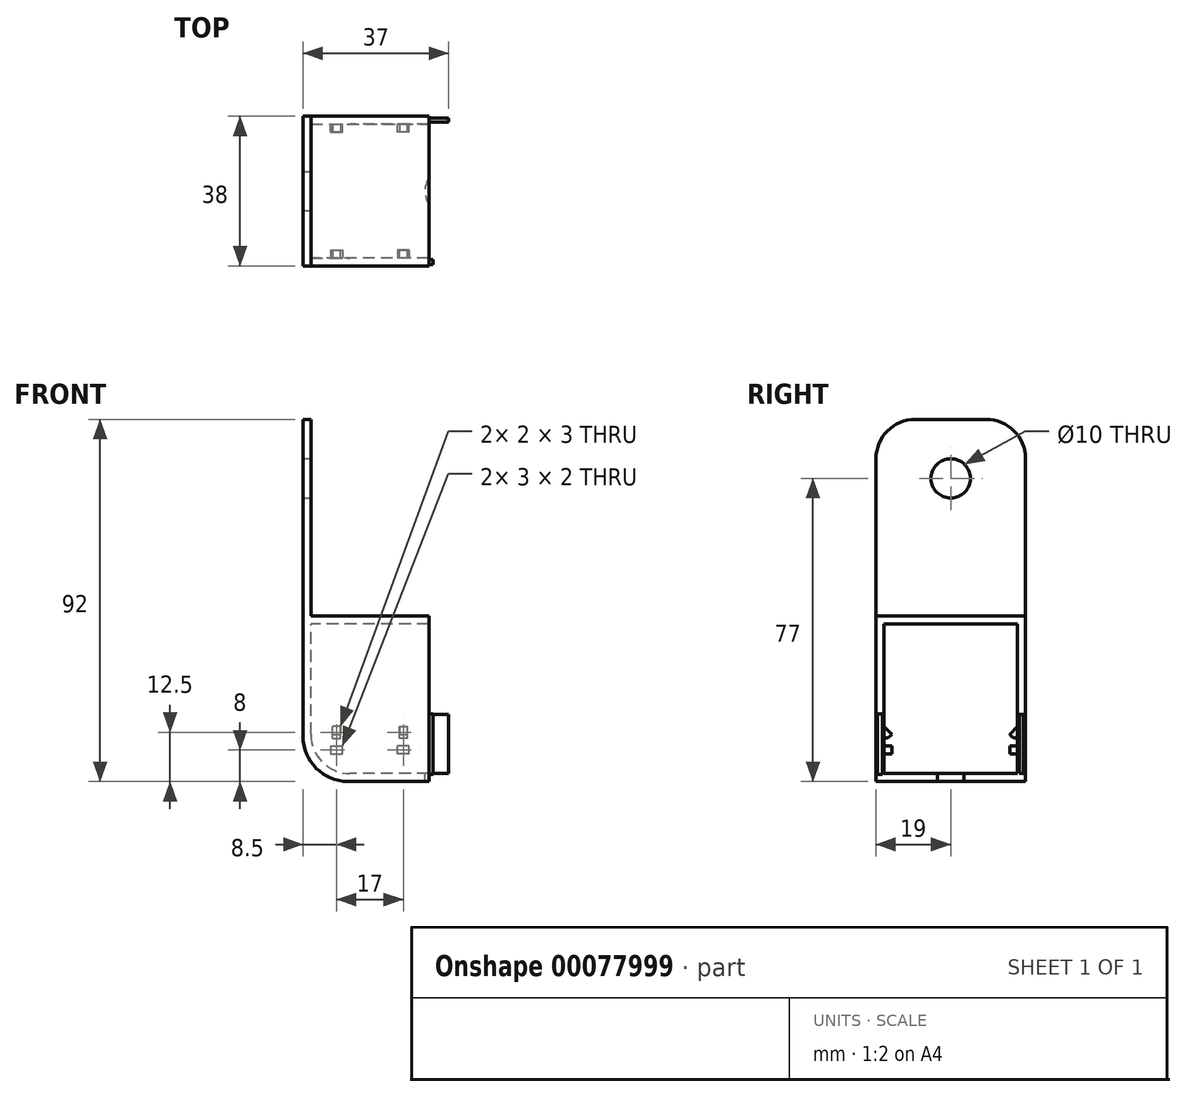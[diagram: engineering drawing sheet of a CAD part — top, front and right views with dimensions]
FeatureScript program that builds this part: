
annotation { "Feature Type Name" : "Feature", "Feature Type Description" : "" }
export const myFeature = defineFeature(function(context is Context, id is Id, definition is map)
    precondition{}
    {
        {
            var Q0;
            Q0=qCreatedBy(makeId("Front.planeOp"),FACE);
            var sketch = newSketch(context, id + "F0", { "sketchPlane" : qUnion([Q0])});
            skLineSegment(sketch, "E0.MirrorCS", {"start": v(-32, 90) * mm, "end": v(-30, 90) * mm});
            skPoint(sketch, "E1.MirrorP", {"position": v(-30, 0) * mm});
            skLineSegment(sketch, "E2.MirrorCS", {"start": v(0, 0) * mm, "end": v(-20, 0) * mm});
            skLineSegment(sketch, "E3.MirrorCS", {"start": v(0, -2) * mm, "end": v(-20.5, -2) * mm});
            skLineSegment(sketch, "E4.MirrorCS", {"start": v(-30, 10) * mm, "end": v(-30, 90) * mm});
            skLineSegment(sketch, "E5.MirrorCS", {"start": v(-32, 9.5) * mm, "end": v(-32, 90) * mm});
            skArc(sketch, "E6.MirrorCS", {"start": v(-20.5, -2) * mm, "mid": v(-28.63, 1.37) * mm, "end": v(-32, 9.5) * mm});
            skPoint(sketch, "E7.MirrorP", {"position": v(-32, -2) * mm});
            skArc(sketch, "E8.MirrorCS", {"start": v(-20, 0) * mm, "mid": v(-27.07, 2.93) * mm, "end": v(-30, 10) * mm});
            skLineSegment(sketch, "E9", {"start": v(0, 0) * mm, "end": v(0, -2) * mm});
            skSolve(sketch);
        }
        {
            var Q0;
            Q0=qSketchRegion(id+"F0",true);
            extrude(context, id + "F1", {"entities" : qUnion([Q0]), "depth" : 38 * mm});
        }
        {
            var Q0;
            Q0=makeQuery(id+"F1.opExtrude","SWEPT_FACE",FACE,{"disambiguationData":[OSD([sQuery(id+"F0.wireOp",EDGE,"Cg1DAzCj-Jl4h-xhaZ-5yM8-POWZ6DaN1KXJ"),sQuery(id+"F0.wireOp",EDGE,"E2.MirrorCS")])]});
            var sketch = newSketch(context, id + "F2", { "sketchPlane" : qUnion([Q0])});
            skLineSegment(sketch, "E10", {"start": v(0, 0) * mm, "end": v(0, -19) * mm, "construction": true});
            skCircle(sketch, "E11", {"center": v(5, -19) * mm, "radius": 6 * mm});
            skLineSegment(sketch, "E12", {"start": v(0, -19) * mm, "end": v(5, -19) * mm, "construction": true});
            skSolve(sketch);
        }
        {
            var Q0;
            Q0=sQuery(id+"F2.wireOp",VERTEX,"E11.center");
            var Q1;
            Q1=makeQuery(id+"F1.opExtrude","SWEPT_BODY",BODY,{"disambiguationData":[OSD([sQuery(id+"F0.wireOp",EDGE,"Cg1DAzCj-Jl4h-xhaZ-5yM8-POWZ6DaN1KXJ"),sQuery(id+"F0.wireOp",EDGE,"Rc3OdnpI-PPKJ-IzEK-crxj-N6ypD6IGL2Ai"),sQuery(id+"F0.wireOp",EDGE,"b85ee0d2-2ca2-42c5-a8c4-3abeb0733db1.0"),sQuery(id+"F0.wireOp",EDGE,"b85ee0d2-2ca2-42c5-a8c4-3abeb0733db1.1"),sQuery(id+"F0.wireOp",EDGE,"gg6dJarn-oOjf-OyDe-YKcx-A4Eh1SBwTlJ6"),sQuery(id+"F0.wireOp",EDGE,"a4d34342-c67a-475b-b215-8b7c6367189b.filletArc"),sQuery(id+"F0.wireOp",EDGE,"1027a92d-97f3-4d37-b9fd-e9bd70ad30d5.filletArc"),sQuery(id+"F0.wireOp",EDGE,"E0.MirrorCS"),sQuery(id+"F0.wireOp",EDGE,"E2.MirrorCS"),sQuery(id+"F0.wireOp",EDGE,"E3.MirrorCS"),sQuery(id+"F0.wireOp",EDGE,"E4.MirrorCS"),sQuery(id+"F0.wireOp",EDGE,"E5.MirrorCS"),sQuery(id+"F0.wireOp",EDGE,"E6.MirrorCS"),sQuery(id+"F0.wireOp",EDGE,"E8.MirrorCS")])]});
            hole(context, id + "F3", {"style" : HoleStyle.SIMPLE, "holeDiameter" : 12 * mm, "endStyle" : HoleEndStyle.THROUGH, "locations" : qUnion([Q0]), "scope" : qUnion([Q1])});
        }
        {
            var Q0;
            Q0=makeQuery(id+"F1.opExtrude","CAP_EDGE",EDGE,{"disambiguationData":[OSD([sQuery(id+"F0.wireOp",EDGE,"E0.MirrorCS")])],"isStart":false});
            var Q1;
            Q1=makeQuery(id+"F1.opExtrude","CAP_EDGE",EDGE,{"disambiguationData":[OSD([sQuery(id+"F0.wireOp",EDGE,"gg6dJarn-oOjf-OyDe-YKcx-A4Eh1SBwTlJ6")])],"isStart":false});
            var Q2;
            Q2=makeQuery(id+"F1.opExtrude","CAP_EDGE",EDGE,{"disambiguationData":[OSD([sQuery(id+"F0.wireOp",EDGE,"E0.MirrorCS")])],"isStart":true});
            var Q3;
            Q3=makeQuery(id+"F1.opExtrude","CAP_EDGE",EDGE,{"disambiguationData":[OSD([sQuery(id+"F0.wireOp",EDGE,"gg6dJarn-oOjf-OyDe-YKcx-A4Eh1SBwTlJ6")])],"isStart":true});
            fillet(context, id + "F4", {"entities" : qUnion([Q0, Q1, Q2, Q3]), "radius" : 10 * mm, "tangentPropagation" : true, "allowEdgeOverflow" : false});
        }
        {
            var Q0;
            Q0=makeQuery(id+"F1.opExtrude","SWEPT_FACE",FACE,{"disambiguationData":[OSD([sQuery(id+"F0.wireOp",EDGE,"E4.MirrorCS")])]});
            var sketch = newSketch(context, id + "F5", { "sketchPlane" : qUnion([Q0])});
            skLineSegment(sketch, "E13", {"start": v(-19, 75) * mm, "end": v(-19, 90) * mm, "construction": true});
            skCircle(sketch, "E14", {"center": v(-19, 75) * mm, "radius": 5 * mm});
            skSolve(sketch);
        }
        {
            var Q0;
            Q0=sQuery(id+"F5.wireOp",VERTEX,"E13.start");
            var Q1;
            Q1=makeQuery(id+"F1.opExtrude","SWEPT_BODY",BODY,{"disambiguationData":[OSD([sQuery(id+"F0.wireOp",EDGE,"Cg1DAzCj-Jl4h-xhaZ-5yM8-POWZ6DaN1KXJ"),sQuery(id+"F0.wireOp",EDGE,"Rc3OdnpI-PPKJ-IzEK-crxj-N6ypD6IGL2Ai"),sQuery(id+"F0.wireOp",EDGE,"b85ee0d2-2ca2-42c5-a8c4-3abeb0733db1.0"),sQuery(id+"F0.wireOp",EDGE,"b85ee0d2-2ca2-42c5-a8c4-3abeb0733db1.1"),sQuery(id+"F0.wireOp",EDGE,"gg6dJarn-oOjf-OyDe-YKcx-A4Eh1SBwTlJ6"),sQuery(id+"F0.wireOp",EDGE,"a4d34342-c67a-475b-b215-8b7c6367189b.filletArc"),sQuery(id+"F0.wireOp",EDGE,"1027a92d-97f3-4d37-b9fd-e9bd70ad30d5.filletArc"),sQuery(id+"F0.wireOp",EDGE,"E0.MirrorCS"),sQuery(id+"F0.wireOp",EDGE,"E2.MirrorCS"),sQuery(id+"F0.wireOp",EDGE,"E3.MirrorCS"),sQuery(id+"F0.wireOp",EDGE,"E4.MirrorCS"),sQuery(id+"F0.wireOp",EDGE,"E5.MirrorCS"),sQuery(id+"F0.wireOp",EDGE,"E6.MirrorCS"),sQuery(id+"F0.wireOp",EDGE,"E8.MirrorCS")])]});
            hole(context, id + "F6", {"style" : HoleStyle.SIMPLE, "holeDiameter" : 10 * mm, "endStyle" : HoleEndStyle.THROUGH, "locations" : qUnion([Q0]), "scope" : qUnion([Q1])});
        }
        {
            var Q0;
            Q0=makeQuery(id+"F1.opExtrude","CAP_FACE",FACE,{"disambiguationData":[OSD([sQuery(id+"F0.wireOp",EDGE,"E0.MirrorCS"),sQuery(id+"F0.wireOp",EDGE,"E2.MirrorCS"),sQuery(id+"F0.wireOp",EDGE,"E3.MirrorCS"),sQuery(id+"F0.wireOp",EDGE,"E4.MirrorCS"),sQuery(id+"F0.wireOp",EDGE,"E5.MirrorCS"),sQuery(id+"F0.wireOp",EDGE,"E6.MirrorCS"),sQuery(id+"F0.wireOp",EDGE,"E8.MirrorCS"),sQuery(id+"F0.wireOp",EDGE,"E9")])],"isStart":false});
            var sketch = newSketch(context, id + "F7", { "sketchPlane" : qUnion([Q0])});
            skLineSegment(sketch, "E15", {"start": v(0, 0) * mm, "end": v(0, 40) * mm});
            skLineSegment(sketch, "E16", {"start": v(0, 40) * mm, "end": v(-30, 40) * mm});
            skLineSegment(sketch, "E17", {"start": v(-30, 40) * mm, "end": v(-30, 10) * mm});
            skLineSegment(sketch, "E18", {"start": v(-20, 0) * mm, "end": v(0, 0) * mm});
            skPoint(sketch, "E19.visualSharp", {"position": v(-30, 0) * mm});
            skArc(sketch, "E19.filletArc", {"start": v(-30, 10) * mm, "mid": v(-27.07, 2.93) * mm, "end": v(-20, 0) * mm});
            skSolve(sketch);
        }
        {
            var Q0;
            Q0=qSketchRegion(id+"F7",true);
            extrude(context, id + "F8", {"entities" : qUnion([Q0]), "oppositeDirection" : true, "depth" : 2 * mm});
        }
        {
            var Q0;
            Q0=makeQuery(id+"F1.opExtrude","CAP_FACE",FACE,{"disambiguationData":[OSD([sQuery(id+"F0.wireOp",EDGE,"E0.MirrorCS"),sQuery(id+"F0.wireOp",EDGE,"E2.MirrorCS"),sQuery(id+"F0.wireOp",EDGE,"E3.MirrorCS"),sQuery(id+"F0.wireOp",EDGE,"E4.MirrorCS"),sQuery(id+"F0.wireOp",EDGE,"E5.MirrorCS"),sQuery(id+"F0.wireOp",EDGE,"E6.MirrorCS"),sQuery(id+"F0.wireOp",EDGE,"E8.MirrorCS"),sQuery(id+"F0.wireOp",EDGE,"E9")])],"isStart":true});
            var sketch = newSketch(context, id + "F9", { "sketchPlane" : qUnion([Q0])});
            skLineSegment(sketch, "E20", {"start": v(0, 0) * mm, "end": v(0, 40) * mm});
            skLineSegment(sketch, "E21", {"start": v(0, 40) * mm, "end": v(30, 40) * mm});
            skLineSegment(sketch, "E22", {"start": v(30, 40) * mm, "end": v(30, 10) * mm});
            skLineSegment(sketch, "E23", {"start": v(20, 0) * mm, "end": v(0, 0) * mm});
            skPoint(sketch, "E24.visualSharp", {"position": v(30, 0) * mm});
            skArc(sketch, "E24.filletArc", {"start": v(20, 0) * mm, "mid": v(27.07, 2.93) * mm, "end": v(30, 10) * mm});
            skSolve(sketch);
        }
        {
            var Q0;
            Q0=qSketchRegion(id+"F9",true);
            extrude(context, id + "F10", {"entities" : qUnion([Q0]), "oppositeDirection" : true, "depth" : 2 * mm});
        }
        {
            var Q0;
            Q0=makeQuery(id+"F10.opExtrude","SWEPT_FACE",FACE,{"disambiguationData":[OSD([sQuery(id+"F9.wireOp",EDGE,"E21")])]});
            var sketch = newSketch(context, id + "F11", { "sketchPlane" : qUnion([Q0])});
            skLineSegment(sketch, "E25", {"start": v(-30, 0) * mm, "end": v(0, 0) * mm});
            skLineSegment(sketch, "E26", {"start": v(0, 0) * mm, "end": v(0, -38) * mm});
            skLineSegment(sketch, "E27", {"start": v(0, -38) * mm, "end": v(-30, -38) * mm});
            skLineSegment(sketch, "E28", {"start": v(-30, -38) * mm, "end": v(-30, 0) * mm});
            skSolve(sketch);
        }
        {
            var Q0;
            Q0=qSketchRegion(id+"F11",true);
            extrude(context, id + "F12", {"entities" : qUnion([Q0]), "oppositeDirection" : true, "depth" : 2 * mm});
        }
        {
            var Q0;
            Q0=makeQuery(id+"F1.opExtrude","SWEPT_BODY",BODY,{"disambiguationData":[OSD([sQuery(id+"F0.wireOp",EDGE,"E0.MirrorCS"),sQuery(id+"F0.wireOp",EDGE,"E2.MirrorCS"),sQuery(id+"F0.wireOp",EDGE,"E3.MirrorCS"),sQuery(id+"F0.wireOp",EDGE,"E4.MirrorCS"),sQuery(id+"F0.wireOp",EDGE,"E5.MirrorCS"),sQuery(id+"F0.wireOp",EDGE,"E6.MirrorCS"),sQuery(id+"F0.wireOp",EDGE,"E8.MirrorCS"),sQuery(id+"F0.wireOp",EDGE,"E9")])]});
            var Q1;
            Q1=makeQuery(id+"F8.opExtrude","SWEPT_BODY",BODY,{"disambiguationData":[OSD([sQuery(id+"F7.wireOp",EDGE,"E15"),sQuery(id+"F7.wireOp",EDGE,"E16"),sQuery(id+"F7.wireOp",EDGE,"E17"),sQuery(id+"F7.wireOp",EDGE,"E18"),sQuery(id+"F7.wireOp",EDGE,"E19.filletArc")])]});
            var Q2;
            Q2=makeQuery(id+"F10.opExtrude","SWEPT_BODY",BODY,{"disambiguationData":[OSD([sQuery(id+"F9.wireOp",EDGE,"E20"),sQuery(id+"F9.wireOp",EDGE,"E21"),sQuery(id+"F9.wireOp",EDGE,"E22"),sQuery(id+"F9.wireOp",EDGE,"E23"),sQuery(id+"F9.wireOp",EDGE,"E24.filletArc")])]});
            var Q3;
            Q3=makeQuery(id+"F12.opExtrude","SWEPT_BODY",BODY,{"disambiguationData":[OSD([sQuery(id+"F11.wireOp",EDGE,"E25"),sQuery(id+"F11.wireOp",EDGE,"E26"),sQuery(id+"F11.wireOp",EDGE,"E27"),sQuery(id+"F11.wireOp",EDGE,"E28")])]});
            booleanBodies(context, id + "F13", {"operationType" : BooleanOperationType.UNION, "tools" : qUnion([Q0, Q1, Q2, Q3])});
        }
        {
            var Q0;
            {var subQ0=sQuery(id+"F0.wireOp",EDGE,"E9");var subQ1=sQuery(id+"F0.wireOp",EDGE,"E8.MirrorCS");var subQ2=sQuery(id+"F0.wireOp",EDGE,"E6.MirrorCS");var subQ3=sQuery(id+"F0.wireOp",EDGE,"E5.MirrorCS");var subQ4=sQuery(id+"F0.wireOp",EDGE,"E4.MirrorCS");var subQ5=sQuery(id+"F0.wireOp",EDGE,"E3.MirrorCS");var subQ6=sQuery(id+"F0.wireOp",EDGE,"E2.MirrorCS");var subQ7=sQuery(id+"F0.wireOp",EDGE,"E0.MirrorCS");var subQ11=makeQuery(id+"F1.opExtrude","SWEPT_FACE",FACE,{"disambiguationData":[OSD([subQ0])]});Q0=makeQuery(id+"F13.opBoolean","MERGE",FACE,{"derivedFrom":[makeQuery(id+"F3.hole-0.boolean.opBoolean","SPLIT",FACE,{"disambiguationData":[TD([makeQuery(id+"F1.opExtrude","CAP_FACE",FACE,{"disambiguationData":[OSD([subQ7,subQ6,subQ5,subQ4,subQ3,subQ2,subQ1,subQ0])],"isStart":true})])],"derivedFrom":subQ11}),makeQuery(id+"F3.hole-0.boolean.opBoolean","SPLIT",FACE,{"disambiguationData":[TD([makeQuery(id+"F1.opExtrude","CAP_FACE",FACE,{"disambiguationData":[OSD([subQ7,subQ6,subQ5,subQ4,subQ3,subQ2,subQ1,subQ0])],"isStart":false})])],"derivedFrom":subQ11}),makeQuery(id+"F8.opExtrude","SWEPT_FACE",FACE,{"disambiguationData":[OSD([sQuery(id+"F7.wireOp",EDGE,"E15")])]}),makeQuery(id+"F10.opExtrude","SWEPT_FACE",FACE,{"disambiguationData":[OSD([sQuery(id+"F9.wireOp",EDGE,"E20")])]}),makeQuery(id+"F12.opExtrude","SWEPT_FACE",FACE,{"disambiguationData":[OSD([sQuery(id+"F11.wireOp",EDGE,"E26")])]})]});}
            var sketch = newSketch(context, id + "F14", { "sketchPlane" : qUnion([Q0])});
            skLineSegment(sketch, "E29", {"start": v(-1, 15) * mm, "end": v(-1, 0) * mm, "construction": true});
            skLineSegment(sketch, "E30", {"start": v(-19, -2) * mm, "end": v(-19, 27.96) * mm, "construction": true});
            skLineSegment(sketch, "E31", {"start": v(-37.65, 15.15) * mm, "end": v(-36.35, 15.15) * mm});
            skLineSegment(sketch, "E32", {"start": v(-1.5, 15) * mm, "end": v(-1.5, 0) * mm});
            skLineSegment(sketch, "E33", {"start": v(-1.5, 0) * mm, "end": v(-0.5, 0) * mm});
            skLineSegment(sketch, "E34", {"start": v(-0.5, 0) * mm, "end": v(-0.5, 15) * mm});
            skLineSegment(sketch, "E35", {"start": v(-0.5, 15) * mm, "end": v(-1.5, 15) * mm});
            skLineSegment(sketch, "E36", {"start": v(-37.65, -0.15) * mm, "end": v(-36.35, -0.15) * mm});
            skLineSegment(sketch, "E37", {"start": v(-37.65, 15.15) * mm, "end": v(-37.65, -0.15) * mm});
            skLineSegment(sketch, "E38", {"start": v(-36.35, -0.15) * mm, "end": v(-36.35, 15.15) * mm});
            skSolve(sketch);
        }
        {
            var Q0;
            Q0=makeQuery(id+"F14.imprint","IMPRINT",FACE,{"disambiguationData":[TD([[makeQuery(id+"F14.imprint","IMPRINT",EDGE,{"derivedFrom":sQuery(id+"F14.wireOp",EDGE,"E32")}),1.0]])]});
            extrude(context, id + "F15", {"entities" : qUnion([Q0]), "operationType" : NewBodyOperationType.ADD, "depth" : 5 * mm});
        }
        {
            var Q0;
            Q0=makeQuery(id+"F10.opExtrude","CAP_FACE",FACE,{"disambiguationData":[OSD([sQuery(id+"F9.wireOp",EDGE,"E20"),sQuery(id+"F9.wireOp",EDGE,"E21"),sQuery(id+"F9.wireOp",EDGE,"E22"),sQuery(id+"F9.wireOp",EDGE,"E23"),sQuery(id+"F9.wireOp",EDGE,"E24.filletArc")])],"isStart":false});
            var sketch = newSketch(context, id + "F16", { "sketchPlane" : qUnion([Q0])});
            skLineSegment(sketch, "E39", {"start": v(-11.63, -4) * mm, "end": v(-30, -4) * mm, "construction": true});
            skLineSegment(sketch, "E40", {"start": v(-25, 6) * mm, "end": v(-25, 7) * mm});
            skLineSegment(sketch, "E41", {"start": v(-25, 7) * mm, "end": v(-22, 7) * mm});
            skLineSegment(sketch, "E42", {"start": v(-25, 6) * mm, "end": v(-25, 5) * mm});
            skLineSegment(sketch, "E43", {"start": v(-25, 5) * mm, "end": v(-22, 5) * mm});
            skLineSegment(sketch, "E44", {"start": v(-22, 5) * mm, "end": v(-22, 7) * mm});
            skLineSegment(sketch, "E45", {"start": v(-25, 7) * mm, "end": v(-25, 9) * mm, "construction": true});
            skLineSegment(sketch, "E46", {"start": v(-30, 7.89) * mm, "end": v(-30, 4.36) * mm, "construction": true});
            skLineSegment(sketch, "E47", {"start": v(-24.5, 9) * mm, "end": v(-22.5, 9) * mm});
            skLineSegment(sketch, "E48", {"start": v(-22.5, 9) * mm, "end": v(-22.5, 12) * mm});
            skLineSegment(sketch, "E49", {"start": v(-22.5, 12) * mm, "end": v(-24.5, 12) * mm});
            skLineSegment(sketch, "E50", {"start": v(-24.5, 9) * mm, "end": v(-24.5, 12) * mm});
            skLineSegment(sketch, "E51", {"start": v(-25, 9) * mm, "end": v(-24.5, 9) * mm, "construction": true});
            skLineSegment(sketch, "E52", {"start": v(-15, 5) * mm, "end": v(-15, 0) * mm, "construction": true});
            skLineSegment(sketch, "E53.MirrorCS", {"start": v(-5, 7) * mm, "end": v(-5, 9) * mm, "construction": true});
            skLineSegment(sketch, "E54.MirrorCS", {"start": v(-5, 9) * mm, "end": v(-5.5, 9) * mm, "construction": true});
            skLineSegment(sketch, "E55.MirrorCS", {"start": v(-5, 6) * mm, "end": v(-5, 5) * mm});
            skLineSegment(sketch, "E56.MirrorCS", {"start": v(-5, 6) * mm, "end": v(-5, 7) * mm});
            skLineSegment(sketch, "E57.MirrorCS", {"start": v(-7.5, 12) * mm, "end": v(-5.5, 12) * mm});
            skLineSegment(sketch, "E58.MirrorCS", {"start": v(-5.5, 9) * mm, "end": v(-7.5, 9) * mm});
            skLineSegment(sketch, "E59.MirrorCS", {"start": v(-7.5, 9) * mm, "end": v(-7.5, 12) * mm});
            skLineSegment(sketch, "E60.MirrorCS", {"start": v(-5.5, 9) * mm, "end": v(-5.5, 12) * mm});
            skLineSegment(sketch, "E61.MirrorCS", {"start": v(-5, 7) * mm, "end": v(-8, 7) * mm});
            skLineSegment(sketch, "E62.MirrorCS", {"start": v(-5, 5) * mm, "end": v(-8, 5) * mm});
            skLineSegment(sketch, "E63.MirrorCS", {"start": v(-8, 5) * mm, "end": v(-8, 7) * mm});
            skLineSegment(sketch, "E64", {"start": v(0, 0) * mm, "end": v(-15, 0) * mm, "construction": true});
            skSolve(sketch);
        }
        {
            var Q0;
            Q0=makeQuery(id+"F8.opExtrude","CAP_FACE",FACE,{"disambiguationData":[OSD([sQuery(id+"F7.wireOp",EDGE,"E15"),sQuery(id+"F7.wireOp",EDGE,"E16"),sQuery(id+"F7.wireOp",EDGE,"E17"),sQuery(id+"F7.wireOp",EDGE,"E18"),sQuery(id+"F7.wireOp",EDGE,"E19.filletArc")])],"isStart":false});
            var sketch = newSketch(context, id + "F17", { "sketchPlane" : qUnion([Q0])});
            skLineSegment(sketch, "E65", {"start": v(10.1, -4) * mm, "end": v(0, -4) * mm, "construction": true});
            skLineSegment(sketch, "E66", {"start": v(5, 6) * mm, "end": v(5, 7) * mm});
            skLineSegment(sketch, "E67", {"start": v(5, 7) * mm, "end": v(8, 7) * mm});
            skLineSegment(sketch, "E68", {"start": v(5, 6) * mm, "end": v(5, 5) * mm});
            skLineSegment(sketch, "E69", {"start": v(5, 5) * mm, "end": v(8, 5) * mm});
            skLineSegment(sketch, "E70", {"start": v(8, 5) * mm, "end": v(8, 7) * mm});
            skLineSegment(sketch, "E71", {"start": v(5, 7) * mm, "end": v(5, 9) * mm, "construction": true});
            skLineSegment(sketch, "E72", {"start": v(0, 13.74) * mm, "end": v(0, 10.22) * mm, "construction": true});
            skLineSegment(sketch, "E73", {"start": v(5.5, 9) * mm, "end": v(7.5, 9) * mm});
            skLineSegment(sketch, "E74", {"start": v(7.5, 9) * mm, "end": v(7.5, 12) * mm});
            skLineSegment(sketch, "E75", {"start": v(7.5, 12) * mm, "end": v(5.5, 12) * mm});
            skLineSegment(sketch, "E76", {"start": v(5.5, 9) * mm, "end": v(5.5, 12) * mm});
            skLineSegment(sketch, "E77", {"start": v(5, 9) * mm, "end": v(5.5, 9) * mm, "construction": true});
            skLineSegment(sketch, "E78", {"start": v(15, 5) * mm, "end": v(15, 0) * mm, "construction": true});
            skLineSegment(sketch, "E79.MirrorCS", {"start": v(25, 7) * mm, "end": v(25, 9) * mm, "construction": true});
            skLineSegment(sketch, "E80.MirrorCS", {"start": v(25, 9) * mm, "end": v(24.5, 9) * mm, "construction": true});
            skLineSegment(sketch, "E81.MirrorCS", {"start": v(25, 6) * mm, "end": v(25, 5) * mm});
            skLineSegment(sketch, "E82.MirrorCS", {"start": v(25, 6) * mm, "end": v(25, 7) * mm});
            skLineSegment(sketch, "E83.MirrorCS", {"start": v(22.5, 12) * mm, "end": v(24.5, 12) * mm});
            skLineSegment(sketch, "E84.MirrorCS", {"start": v(24.5, 9) * mm, "end": v(22.5, 9) * mm});
            skLineSegment(sketch, "E85.MirrorCS", {"start": v(22.5, 9) * mm, "end": v(22.5, 12) * mm});
            skLineSegment(sketch, "E86.MirrorCS", {"start": v(24.5, 9) * mm, "end": v(24.5, 12) * mm});
            skLineSegment(sketch, "E87.MirrorCS", {"start": v(25, 7) * mm, "end": v(22, 7) * mm});
            skLineSegment(sketch, "E88.MirrorCS", {"start": v(25, 5) * mm, "end": v(22, 5) * mm});
            skLineSegment(sketch, "E89.MirrorCS", {"start": v(22, 5) * mm, "end": v(22, 7) * mm});
            skLineSegment(sketch, "E90", {"start": v(0, 0) * mm, "end": v(15, 0) * mm, "construction": true});
            skSolve(sketch);
        }
        {
            var Q0;
            Q0=makeQuery(id+"F16.imprint","IMPRINT",FACE,{"disambiguationData":[TD([[makeQuery(id+"F16.imprint","IMPRINT",EDGE,{"derivedFrom":sQuery(id+"F16.wireOp",EDGE,"E57.MirrorCS")}),-1.0]])]});
            var Q1;
            Q1=makeQuery(id+"F16.imprint","IMPRINT",FACE,{"disambiguationData":[TD([[makeQuery(id+"F16.imprint","IMPRINT",EDGE,{"derivedFrom":sQuery(id+"F16.wireOp",EDGE,"E55.MirrorCS")}),-1.0]])]});
            var Q2;
            Q2=makeQuery(id+"F16.imprint","IMPRINT",FACE,{"disambiguationData":[TD([[makeQuery(id+"F16.imprint","IMPRINT",EDGE,{"derivedFrom":sQuery(id+"F16.wireOp",EDGE,"E47")}),1.0]])]});
            var Q3;
            Q3=makeQuery(id+"F16.imprint","IMPRINT",FACE,{"disambiguationData":[TD([[makeQuery(id+"F16.imprint","IMPRINT",EDGE,{"derivedFrom":sQuery(id+"F16.wireOp",EDGE,"E40")}),-1.0]])]});
            extrude(context, id + "F18", {"entities" : qUnion([Q0, Q1, Q2, Q3]), "operationType" : NewBodyOperationType.ADD, "depth" : 2 * mm});
        }
        {
            var Q0;
            Q0=makeQuery(id+"F17.imprint","IMPRINT",FACE,{"disambiguationData":[TD([[makeQuery(id+"F17.imprint","IMPRINT",EDGE,{"derivedFrom":sQuery(id+"F17.wireOp",EDGE,"E73")}),1.0]])]});
            var Q1;
            Q1=makeQuery(id+"F17.imprint","IMPRINT",FACE,{"disambiguationData":[TD([[makeQuery(id+"F17.imprint","IMPRINT",EDGE,{"derivedFrom":sQuery(id+"F17.wireOp",EDGE,"E66")}),-1.0]])]});
            var Q2;
            Q2=makeQuery(id+"F17.imprint","IMPRINT",FACE,{"disambiguationData":[TD([[makeQuery(id+"F17.imprint","IMPRINT",EDGE,{"derivedFrom":sQuery(id+"F17.wireOp",EDGE,"E81.MirrorCS")}),-1.0]])]});
            var Q3;
            Q3=makeQuery(id+"F17.imprint","IMPRINT",FACE,{"disambiguationData":[TD([[makeQuery(id+"F17.imprint","IMPRINT",EDGE,{"derivedFrom":sQuery(id+"F17.wireOp",EDGE,"E83.MirrorCS")}),-1.0]])]});
            extrude(context, id + "F19", {"entities" : qUnion([Q0, Q1, Q2, Q3]), "operationType" : NewBodyOperationType.ADD, "depth" : 2 * mm});
        }
        {
            var Q0;
            Q0=makeQuery(id+"F19.opExtrude","CAP_EDGE",EDGE,{"disambiguationData":[OSD([sQuery(id+"F17.wireOp",EDGE,"E75")])],"isStart":false});
            var Q1;
            Q1=makeQuery(id+"F19.opExtrude","CAP_EDGE",EDGE,{"disambiguationData":[OSD([sQuery(id+"F17.wireOp",EDGE,"E83.MirrorCS")])],"isStart":false});
            var Q2;
            Q2=makeQuery(id+"F18.opExtrude","CAP_EDGE",EDGE,{"disambiguationData":[OSD([sQuery(id+"F16.wireOp",EDGE,"E57.MirrorCS")])],"isStart":false});
            var Q3;
            Q3=makeQuery(id+"F18.opExtrude","CAP_EDGE",EDGE,{"disambiguationData":[OSD([sQuery(id+"F16.wireOp",EDGE,"E49")])],"isStart":false});
            chamfer(context, id + "F20", {"entities" : qUnion([Q0, Q1, Q2, Q3]), "width" : 2 * mm, "tangentPropagation" : true});
        }
        {
            var Q0;
            Q0=makeQuery(id+"F19.opExtrude","CAP_EDGE",EDGE,{"disambiguationData":[OSD([sQuery(id+"F17.wireOp",EDGE,"E73")])],"isStart":false});
            var Q1;
            Q1=makeQuery(id+"F19.opExtrude","CAP_EDGE",EDGE,{"disambiguationData":[OSD([sQuery(id+"F17.wireOp",EDGE,"E84.MirrorCS")])],"isStart":false});
            var Q2;
            Q2=makeQuery(id+"F18.opExtrude","CAP_EDGE",EDGE,{"disambiguationData":[OSD([sQuery(id+"F16.wireOp",EDGE,"E58.MirrorCS")])],"isStart":false});
            var Q3;
            Q3=makeQuery(id+"F18.opExtrude","CAP_EDGE",EDGE,{"disambiguationData":[OSD([sQuery(id+"F16.wireOp",EDGE,"E47")])],"isStart":false});
            fillet(context, id + "F21", {"entities" : qUnion([Q0, Q1, Q2, Q3]), "radius" : 2 * mm, "tangentPropagation" : true, "allowEdgeOverflow" : false});
        }
        {
            var Q0;
            Q0=makeQuery(id+"F14.imprint","IMPRINT",FACE,{"disambiguationData":[TD([[makeQuery(id+"F14.imprint","IMPRINT",EDGE,{"derivedFrom":sQuery(id+"F14.wireOp",EDGE,"E31")}),-1.0]])]});
            extrude(context, id + "F22", {"entities" : qUnion([Q0]), "operationType" : NewBodyOperationType.ADD, "depth" : 1 * mm});
        }
    });
